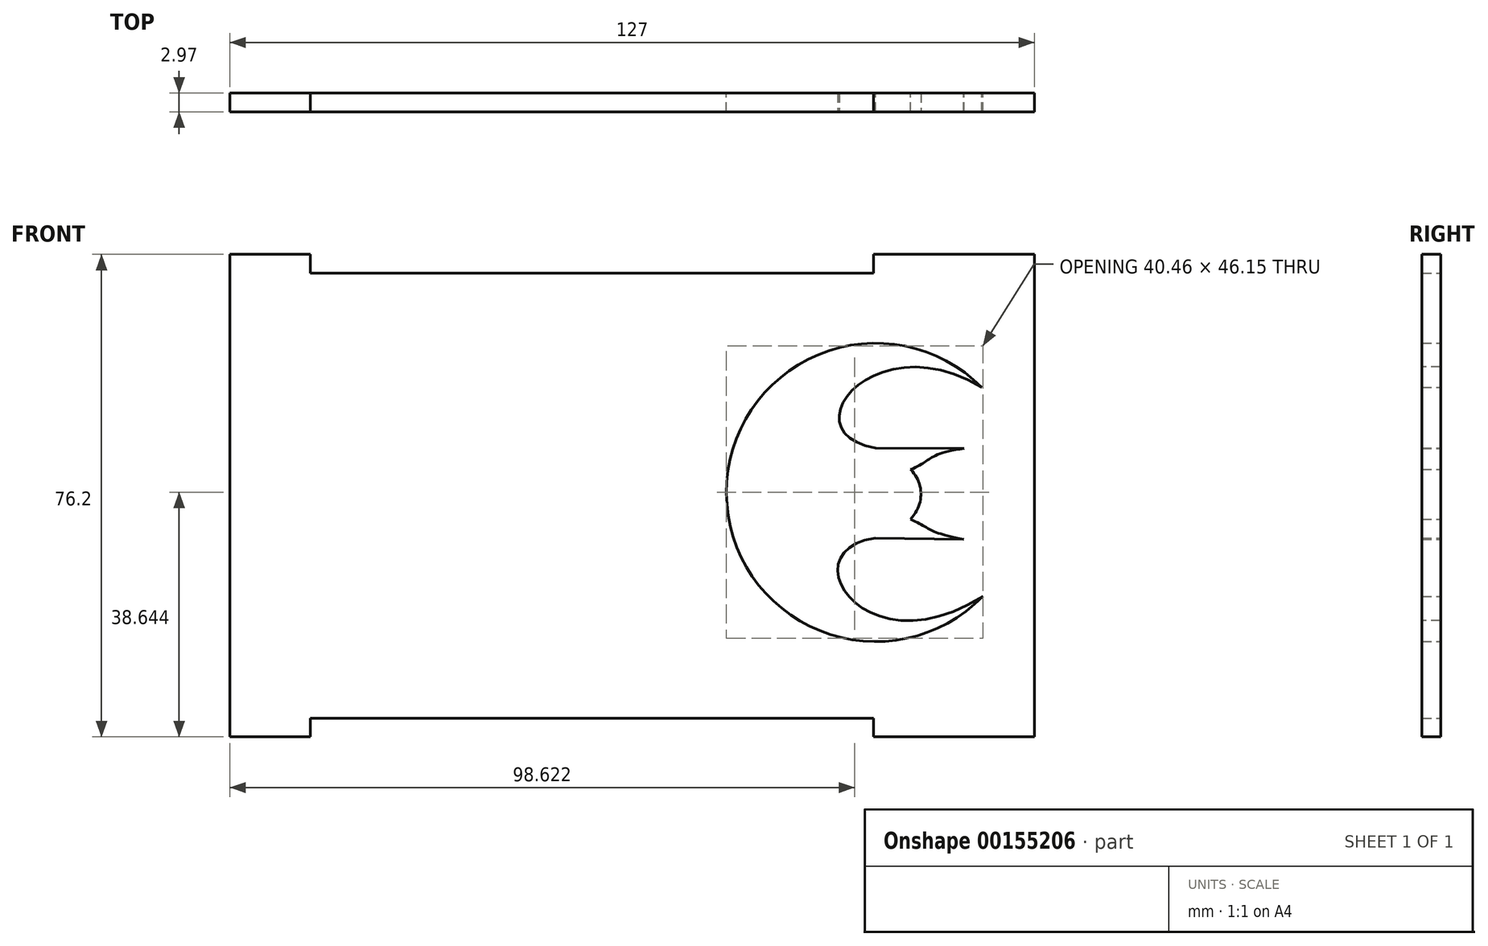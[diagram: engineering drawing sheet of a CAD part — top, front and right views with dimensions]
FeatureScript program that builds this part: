
annotation { "Feature Type Name" : "Feature", "Feature Type Description" : "" }
export const myFeature = defineFeature(function(context is Context, id is Id, definition is map)
    precondition{}
    {
        {
            var Q0;
            Q0=qCreatedBy(makeId("Front.planeOp"),FACE);
            var sketch = newSketch(context, id + "F0", { "sketchPlane" : qUnion([Q0])});
            skLineSegment(sketch, "E0.bottom", {"start": v(-126.78, 29.55) * mm, "end": v(0.22, 29.55) * mm});
            skLineSegment(sketch, "E0.top", {"start": v(-126.78, -46.65) * mm, "end": v(0.22, -46.65) * mm});
            skLineSegment(sketch, "E0.left", {"start": v(-126.78, 29.55) * mm, "end": v(-126.78, -46.65) * mm});
            skLineSegment(sketch, "E0.right", {"start": v(0.22, 29.55) * mm, "end": v(0.22, -46.65) * mm});
            skLineSegment(sketch, "E1.bottom", {"start": v(-114.08, 29.55) * mm, "end": v(-25.18, 29.55) * mm});
            skLineSegment(sketch, "E1.top", {"start": v(-114.08, 26.58) * mm, "end": v(-25.18, 26.58) * mm});
            skLineSegment(sketch, "E1.left", {"start": v(-114.08, 29.55) * mm, "end": v(-114.08, 26.58) * mm});
            skLineSegment(sketch, "E1.right", {"start": v(-25.18, 29.55) * mm, "end": v(-25.18, 26.58) * mm});
            skLineSegment(sketch, "E2.bottom", {"start": v(-114.08, -46.65) * mm, "end": v(-25.18, -46.65) * mm});
            skLineSegment(sketch, "E2.top", {"start": v(-114.08, -43.68) * mm, "end": v(-25.18, -43.68) * mm});
            skLineSegment(sketch, "E2.left", {"start": v(-114.08, -46.65) * mm, "end": v(-114.08, -43.68) * mm});
            skLineSegment(sketch, "E2.right", {"start": v(-25.18, -46.65) * mm, "end": v(-25.18, -43.68) * mm});
            skLineSegment(sketch, "E3.bottom", {"start": v(-108.8, 16.45) * mm, "end": v(-58.8, 16.45) * mm});
            skLineSegment(sketch, "E3.top", {"start": v(-108.8, -33.55) * mm, "end": v(-58.8, -33.55) * mm});
            skLineSegment(sketch, "E3.left", {"start": v(-108.8, 16.45) * mm, "end": v(-108.8, -33.55) * mm});
            skLineSegment(sketch, "E3.right", {"start": v(-58.8, 16.45) * mm, "end": v(-58.8, -33.55) * mm});
            skFitSpline(sketch, "E4", {"points": [v(8.8, 268.47) * mm, v(17.92, 251.44) * mm], "startDerivative": vector(-35.8, -55.66) * mm, "endDerivative": vector(6.1, 41.2) * mm});
            skLineSegment(sketch, "E5", {"start": v(17.77, 265.4) * mm, "end": v(17.92, 251.44) * mm});
            skLineSegment(sketch, "E6", {"start": v(32.15, 265.4) * mm, "end": v(32.15, 251.43) * mm});
            skFitSpline(sketch, "E7", {"points": [v(32.15, 251.43) * mm, v(41.8, 268.11) * mm], "startDerivative": vector(6.65, -41.8) * mm, "endDerivative": vector(-30.57, 51.52) * mm});
            skFitSpline(sketch, "E8", {"points": [v(17.77, 265.4) * mm, v(20.93, 256.98) * mm], "startDerivative": vector(3, -16.36) * mm, "endDerivative": vector(4.42, -9.66) * mm});
            skFitSpline(sketch, "E9", {"points": [v(32.15, 265.4) * mm, v(28.78, 256.98) * mm], "startDerivative": vector(-2.53, -17.55) * mm, "endDerivative": vector(-3.82, -9.66) * mm});
            skFitSpline(sketch, "E10", {"points": [v(20.93, 256.98) * mm, v(28.78, 256.98) * mm], "startDerivative": vector(7.35, 6.66) * mm, "endDerivative": vector(6.78, -6.43) * mm});
            skArc(sketch, "E11", {"start": v(8.8, 268.47) * mm, "mid": v(24.87, 227.92) * mm, "end": v(41.8, 268.11) * mm});
            skLineSegment(sketch, "E12", {"start": v(23.2, 320.42) * mm, "end": v(-78.96, 218.82) * mm});
            skFitSpline(sketch, "E13.MirrorCS", {"points": [v(20.93, 383.86) * mm, v(28.78, 383.86) * mm], "startDerivative": vector(7.35, -6.66) * mm, "endDerivative": vector(6.78, 6.43) * mm});
            skLineSegment(sketch, "E14.MirrorCS", {"start": v(32.15, 375.44) * mm, "end": v(32.15, 389.4) * mm});
            skLineSegment(sketch, "E15.MirrorCS", {"start": v(17.77, 375.44) * mm, "end": v(17.92, 389.4) * mm});
            skFitSpline(sketch, "E16.MirrorCS", {"points": [v(17.77, 375.44) * mm, v(20.93, 383.86) * mm], "startDerivative": vector(3, 16.36) * mm, "endDerivative": vector(4.42, 9.66) * mm});
            skFitSpline(sketch, "E17.MirrorCS", {"points": [v(32.15, 375.44) * mm, v(28.78, 383.86) * mm], "startDerivative": vector(-2.53, 17.55) * mm, "endDerivative": vector(-3.82, 9.66) * mm});
            skFitSpline(sketch, "E18.MirrorCS", {"points": [v(8.8, 372.37) * mm, v(17.92, 389.4) * mm], "startDerivative": vector(-35.8, 55.66) * mm, "endDerivative": vector(6.1, -41.2) * mm});
            skFitSpline(sketch, "E19.MirrorCS", {"points": [v(32.15, 389.4) * mm, v(41.8, 372.73) * mm], "startDerivative": vector(6.65, 41.8) * mm, "endDerivative": vector(-30.57, -51.52) * mm});
            skArc(sketch, "E20.MirrorCS", {"start": v(8.8, 372.37) * mm, "mid": v(24.87, 412.92) * mm, "end": v(41.8, 372.73) * mm});
            skFitSpline(sketch, "E21.MirrorCS", {"points": [v(-40.24, 318.5) * mm, v(-40.2, 326.34) * mm], "startDerivative": vector(6.7, 7.3) * mm, "endDerivative": vector(-6.39, 6.82) * mm});
            skLineSegment(sketch, "E22.MirrorCS", {"start": v(-31.84, 315.29) * mm, "end": v(-45.8, 315.52) * mm});
            skFitSpline(sketch, "E23.MirrorCS", {"points": [v(-31.84, 315.29) * mm, v(-40.24, 318.5) * mm], "startDerivative": vector(-16.34, 3.08) * mm, "endDerivative": vector(-9.63, 4.47) * mm});
            skFitSpline(sketch, "E24.MirrorCS", {"points": [v(-31.76, 329.66) * mm, v(-40.2, 326.34) * mm], "startDerivative": vector(-17.56, -2.43) * mm, "endDerivative": vector(-9.68, -3.77) * mm});
            skLineSegment(sketch, "E25.MirrorCS", {"start": v(-31.76, 329.66) * mm, "end": v(-45.73, 329.74) * mm});
            skFitSpline(sketch, "E26.MirrorCS", {"points": [v(-28.82, 306.3) * mm, v(-45.8, 315.52) * mm], "startDerivative": vector(-55.85, -35.5) * mm, "endDerivative": vector(41.23, 5.87) * mm});
            skFitSpline(sketch, "E27.MirrorCS", {"points": [v(-45.73, 329.74) * mm, v(-29, 339.31) * mm], "startDerivative": vector(-41.76, 6.88) * mm, "endDerivative": vector(51.35, -30.86) * mm});
            skArc(sketch, "E28.MirrorCS", {"start": v(-28.82, 306.3) * mm, "mid": v(-69.29, 322.6) * mm, "end": v(-29, 339.31) * mm});
            skFitSpline(sketch, "E29.MirrorCS", {"points": [v(8.8, 268.47) * mm, v(17.92, 251.44) * mm], "startDerivative": vector(-35.8, -55.66) * mm, "endDerivative": vector(6.1, 41.2) * mm});
            skFitSpline(sketch, "E30.MirrorCS", {"points": [v(-292.85, 259) * mm, v(-309.83, 268.22) * mm], "startDerivative": vector(-55.85, -35.5) * mm, "endDerivative": vector(41.23, 5.87) * mm});
            skLineSegment(sketch, "E31.MirrorCS", {"start": v(-295.87, 267.99) * mm, "end": v(-309.83, 268.22) * mm});
            skLineSegment(sketch, "E32.MirrorCS", {"start": v(-295.79, 282.36) * mm, "end": v(-309.76, 282.44) * mm});
            skFitSpline(sketch, "E33.MirrorCS", {"points": [v(-309.76, 282.44) * mm, v(-293.02, 292.01) * mm], "startDerivative": vector(-41.76, 6.88) * mm, "endDerivative": vector(51.35, -30.86) * mm});
            skFitSpline(sketch, "E34.MirrorCS", {"points": [v(-295.87, 267.99) * mm, v(-304.27, 271.2) * mm], "startDerivative": vector(-16.34, 3.08) * mm, "endDerivative": vector(-9.63, 4.47) * mm});
            skFitSpline(sketch, "E35.MirrorCS", {"points": [v(-295.79, 282.36) * mm, v(-304.23, 279.04) * mm], "startDerivative": vector(-17.56, -2.43) * mm, "endDerivative": vector(-9.68, -3.77) * mm});
            skFitSpline(sketch, "E36.MirrorCS", {"points": [v(-304.27, 271.2) * mm, v(-304.23, 279.04) * mm], "startDerivative": vector(6.7, 7.3) * mm, "endDerivative": vector(-6.39, 6.82) * mm});
            skFitSpline(sketch, "E37.MirrorCS", {"points": [v(-19.35, -12.26) * mm, v(-19.3, -4.4) * mm], "startDerivative": vector(6.7, 7.3) * mm, "endDerivative": vector(-6.39, 6.82) * mm});
            skLineSegment(sketch, "E38.MirrorCS", {"start": v(-10.94, -15.46) * mm, "end": v(-24.91, -15.23) * mm});
            skFitSpline(sketch, "E39.MirrorCS", {"points": [v(-10.94, -15.46) * mm, v(-19.35, -12.26) * mm], "startDerivative": vector(-16.34, 3.08) * mm, "endDerivative": vector(-9.63, 4.47) * mm});
            skFitSpline(sketch, "E40.MirrorCS", {"points": [v(-10.86, -1.09) * mm, v(-19.3, -4.4) * mm], "startDerivative": vector(-17.56, -2.43) * mm, "endDerivative": vector(-9.68, -3.77) * mm});
            skLineSegment(sketch, "E41.MirrorCS", {"start": v(-10.86, -1.09) * mm, "end": v(-24.83, -1) * mm});
            skFitSpline(sketch, "E42.MirrorCS", {"points": [v(-7.93, -24.44) * mm, v(-24.91, -15.23) * mm], "startDerivative": vector(-55.85, -35.5) * mm, "endDerivative": vector(41.23, 5.87) * mm});
            skFitSpline(sketch, "E43.MirrorCS", {"points": [v(-24.83, -1) * mm, v(-8.1, 8.56) * mm], "startDerivative": vector(-41.76, 6.88) * mm, "endDerivative": vector(51.35, -30.86) * mm});
            skArc(sketch, "E44.MirrorCS", {"start": v(-7.93, -24.44) * mm, "mid": v(-48.4, -8.16) * mm, "end": v(-8.1, 8.56) * mm});
            skSolve(sketch);
        }
        {
            var Q0;
            {var subQ0=sQuery(id+"F0.wireOp",EDGE,"E0.left");Q0=makeQuery(id+"F0.imprint","IMPRINT",FACE,{"disambiguationData":[TD([[makeQuery(id+"F0.imprint","IMPRINT",EDGE,{"derivedFrom":subQ0}),1.0]])]});}
            var Q1;
            Q1=makeQuery(id+"F0.imprint","IMPRINT",FACE,{"disambiguationData":[TD([[makeQuery(id+"F0.imprint","IMPRINT",EDGE,{"derivedFrom":sQuery(id+"F0.wireOp",EDGE,"E3.bottom")}),-1.0]])]});
            extrude(context, id + "F1", {"entities" : qUnion([Q0, Q1]), "depth" : 2.97 * mm});
        }
    });
